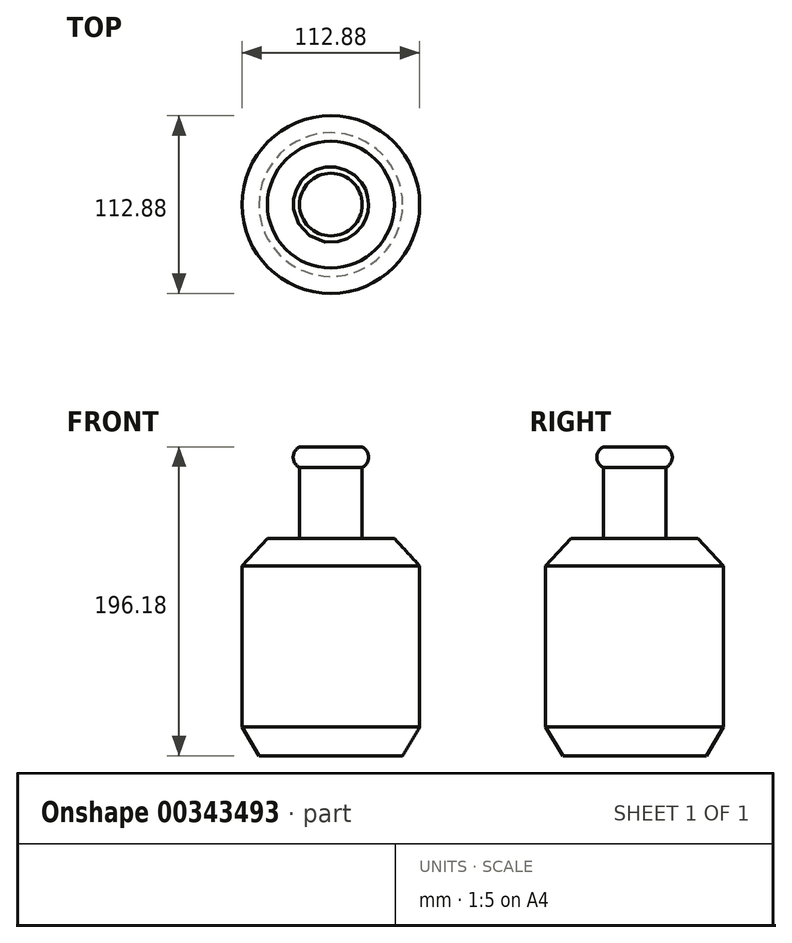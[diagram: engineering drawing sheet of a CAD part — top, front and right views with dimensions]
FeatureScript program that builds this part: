
annotation { "Feature Type Name" : "Feature", "Feature Type Description" : "" }
export const myFeature = defineFeature(function(context is Context, id is Id, definition is map)
    precondition{}
    {
        {
            var Q0;
            Q0=qCreatedBy(makeId("Front.planeOp"),FACE);
            var sketch = newSketch(context, id + "F0", { "sketchPlane" : qUnion([Q0])});
            skLineSegment(sketch, "E0", {"start": v(0, 0) * mm, "end": v(45.62, 0) * mm});
            skLineSegment(sketch, "E1", {"start": v(45.62, 0) * mm, "end": v(56.44, 18.32) * mm});
            skLineSegment(sketch, "E2", {"start": v(56.44, 18.32) * mm, "end": v(56.44, 120.61) * mm});
            skLineSegment(sketch, "E3", {"start": v(56.44, 120.61) * mm, "end": v(40.29, 138.09) * mm});
            skLineSegment(sketch, "E4", {"start": v(40.29, 138.09) * mm, "end": v(19.9, 138.09) * mm});
            skLineSegment(sketch, "E5", {"start": v(19.9, 138.09) * mm, "end": v(19.9, 183.13) * mm});
            skArc(sketch, "E6", {"start": v(19.9, 183.13) * mm, "mid": v(23.94, 189.65) * mm, "end": v(19.9, 196.18) * mm});
            skLineSegment(sketch, "E7", {"start": v(19.9, 196.18) * mm, "end": v(0, 196.18) * mm});
            skLineSegment(sketch, "E8", {"start": v(0, 196.18) * mm, "end": v(0, 0) * mm});
            skSolve(sketch);
        }
        {
            var Q0;
            Q0 = qSketchRegion(id + "F0", true);
            var Q1;
            Q1=sQuery(id+"F0.wireOp",EDGE,"E8");
            revolve(context, id + "F1", {"entities" : qUnion([Q0]), "axis" : qUnion([Q1]), "revolveType" : RevolveType.FULL});
        }
    });
